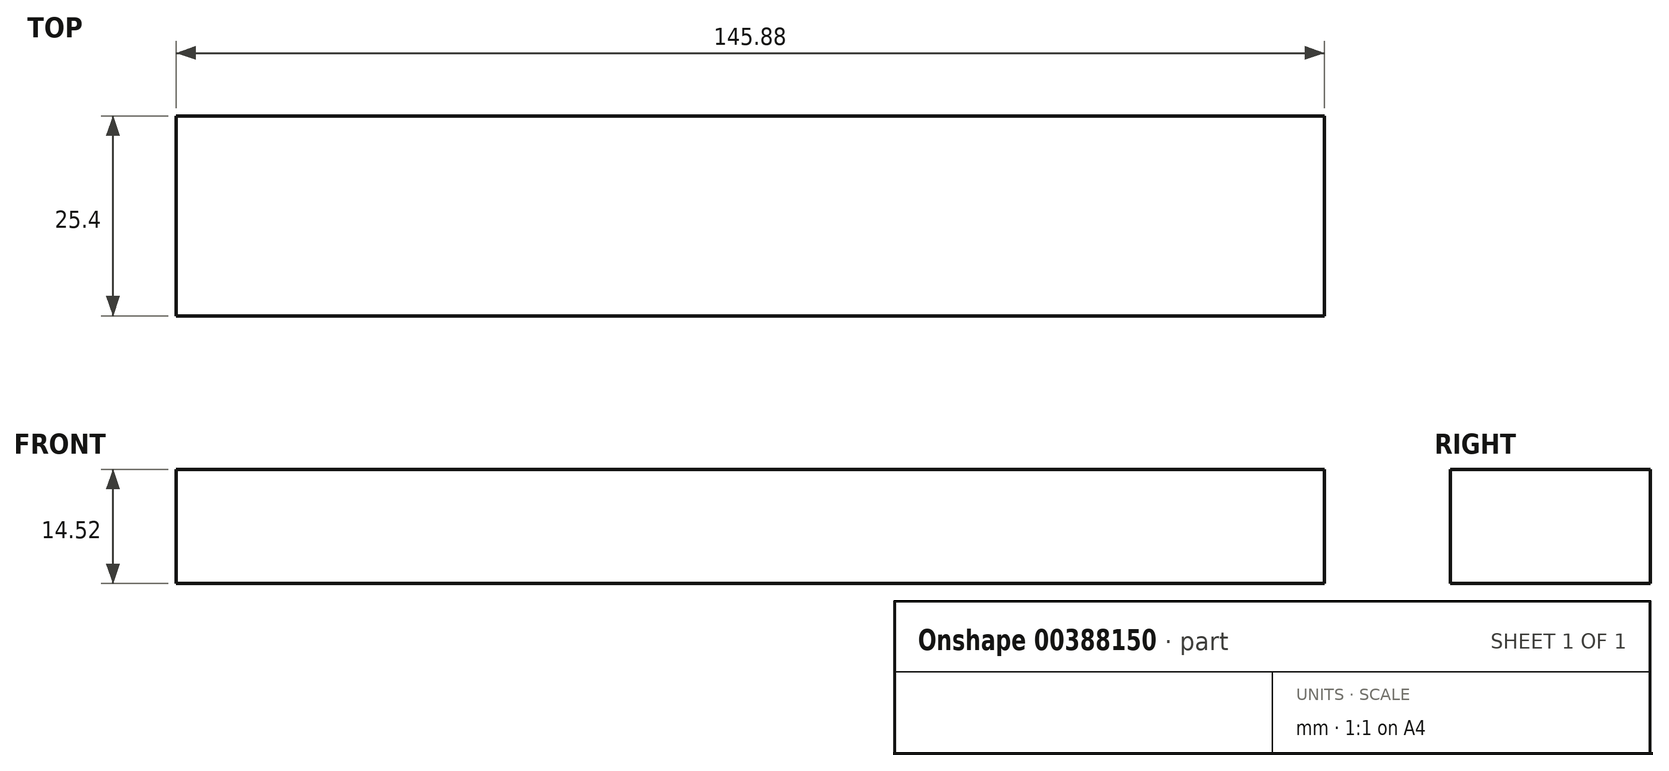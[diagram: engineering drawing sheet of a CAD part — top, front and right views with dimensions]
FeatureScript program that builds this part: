
annotation { "Feature Type Name" : "Feature", "Feature Type Description" : "" }
export const myFeature = defineFeature(function(context is Context, id is Id, definition is map)
    precondition{}
    {
        {
            var Q0;
            Q0=qCreatedBy(makeId("Front.planeOp"),FACE);
            var sketch = newSketch(context, id + "F0", { "sketchPlane" : qUnion([Q0])});
            skLineSegment(sketch, "E0.bottom", {"start": v(-72.94, 7.26) * mm, "end": v(72.94, 7.26) * mm});
            skLineSegment(sketch, "E0.top", {"start": v(-72.94, -7.26) * mm, "end": v(72.94, -7.26) * mm});
            skLineSegment(sketch, "E0.left", {"start": v(-72.94, 7.26) * mm, "end": v(-72.94, -7.26) * mm});
            skLineSegment(sketch, "E0.right", {"start": v(72.94, 7.26) * mm, "end": v(72.94, -7.26) * mm});
            skPoint(sketch, "E0.middle", {"position": v(0, 0) * mm});
            skSolve(sketch);
        }
        {
            var Q0;
            Q0=makeQuery(id+"F0.imprint","IMPRINT",FACE,{"disambiguationData":[TD([[makeQuery(id+"F0.imprint","IMPRINT",EDGE,{"derivedFrom":sQuery(id+"F0.wireOp",EDGE,"E0.bottom")}),-1.0]])]});
            extrude(context, id + "F1", {"entities" : qUnion([Q0]), "depth" : 25.4 * mm});
        }
    });
